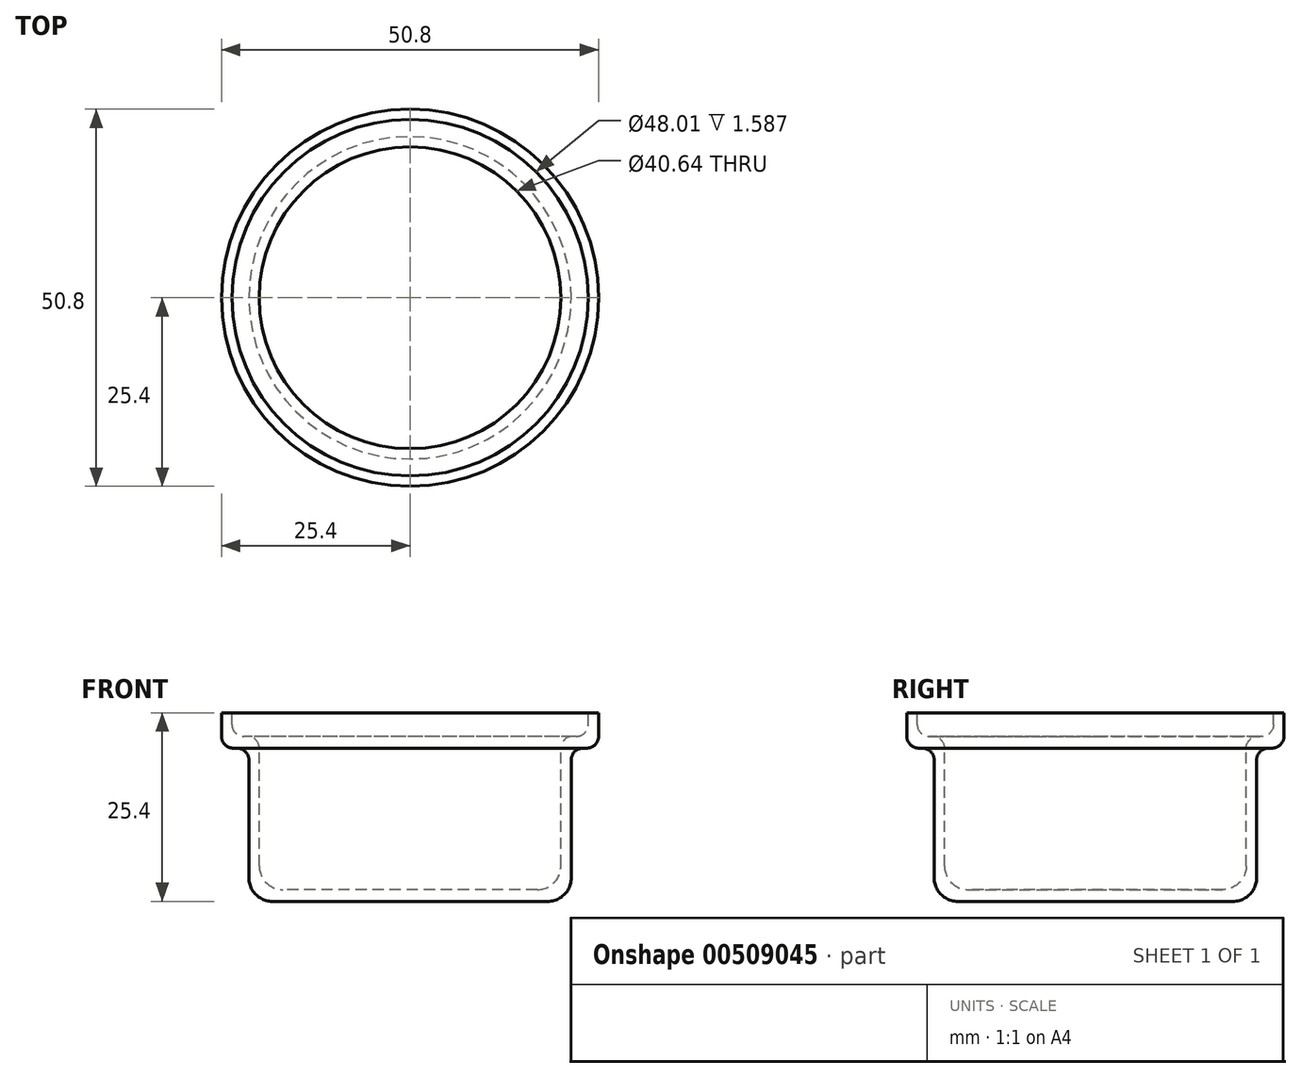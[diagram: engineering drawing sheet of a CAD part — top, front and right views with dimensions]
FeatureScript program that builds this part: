
annotation { "Feature Type Name" : "Feature", "Feature Type Description" : "" }
export const myFeature = defineFeature(function(context is Context, id is Id, definition is map)
    precondition{}
    {
        {
            var Q0;
            Q0=qCreatedBy(makeId("Front.planeOp"),FACE);
            var sketch = newSketch(context, id + "F0", { "sketchPlane" : qUnion([Q0])});
            skLineSegment(sketch, "E0", {"start": v(0, 0) * mm, "end": v(18.54, 0) * mm});
            skLineSegment(sketch, "E1", {"start": v(21.72, 3.18) * mm, "end": v(21.72, 19.05) * mm});
            skLineSegment(sketch, "E2", {"start": v(23.3, 20.64) * mm, "end": v(23.81, 20.64) * mm});
            skLineSegment(sketch, "E3", {"start": v(25.4, 22.23) * mm, "end": v(25.4, 25.4) * mm});
            skLineSegment(sketch, "E4", {"start": v(25.4, 25.4) * mm, "end": v(24, 25.4) * mm});
            skLineSegment(sketch, "E5", {"start": v(24, 25.4) * mm, "end": v(24, 23.81) * mm});
            skLineSegment(sketch, "E6", {"start": v(22.42, 22.23) * mm, "end": v(21.9, 22.23) * mm});
            skLineSegment(sketch, "E7", {"start": v(20.32, 20.64) * mm, "end": v(20.32, 4.76) * mm});
            skLineSegment(sketch, "E8", {"start": v(17.15, 1.59) * mm, "end": v(0, 1.59) * mm});
            skLineSegment(sketch, "E9", {"start": v(0, 1.59) * mm, "end": v(0, 0) * mm});
            skPoint(sketch, "E10.visualSharp", {"position": v(25.4, 20.64) * mm});
            skArc(sketch, "E10.filletArc", {"start": v(23.81, 20.64) * mm, "mid": v(24.94, 21.1) * mm, "end": v(25.4, 22.23) * mm});
            skPoint(sketch, "E11.visualSharp", {"position": v(24, 22.23) * mm});
            skArc(sketch, "E11.filletArc", {"start": v(22.42, 22.22) * mm, "mid": v(23.54, 22.69) * mm, "end": v(24, 23.81) * mm});
            skPoint(sketch, "E12.visualSharp", {"position": v(21.72, 20.64) * mm});
            skArc(sketch, "E12.filletArc", {"start": v(23.3, 20.64) * mm, "mid": v(22.18, 20.17) * mm, "end": v(21.72, 19.05) * mm});
            skPoint(sketch, "E13.visualSharp", {"position": v(20.32, 22.22) * mm});
            skArc(sketch, "E13.filletArc", {"start": v(21.9, 22.22) * mm, "mid": v(20.78, 21.76) * mm, "end": v(20.32, 20.64) * mm});
            skPoint(sketch, "E14.visualSharp", {"position": v(21.72, 0) * mm});
            skArc(sketch, "E14.filletArc", {"start": v(18.54, 0) * mm, "mid": v(20.79, 0.93) * mm, "end": v(21.72, 3.18) * mm});
            skPoint(sketch, "E15.visualSharp", {"position": v(20.32, 1.59) * mm});
            skArc(sketch, "E15.filletArc", {"start": v(17.15, 1.59) * mm, "mid": v(19.4, 2.52) * mm, "end": v(20.32, 4.76) * mm});
            skSolve(sketch);
        }
        {
            var Q0;
            Q0=makeQuery(id+"F0.imprint","IMPRINT",FACE,{"disambiguationData":[TD([[makeQuery(id+"F0.imprint","IMPRINT",EDGE,{"derivedFrom":sQuery(id+"F0.wireOp",EDGE,"E0")}),1.0]])]});
            var Q1;
            Q1=sQuery(id+"F0.wireOp",EDGE,"E9");
            revolve(context, id + "F1", {"entities" : qUnion([Q0]), "axis" : qUnion([Q1]), "revolveType" : RevolveType.FULL});
        }
    });
